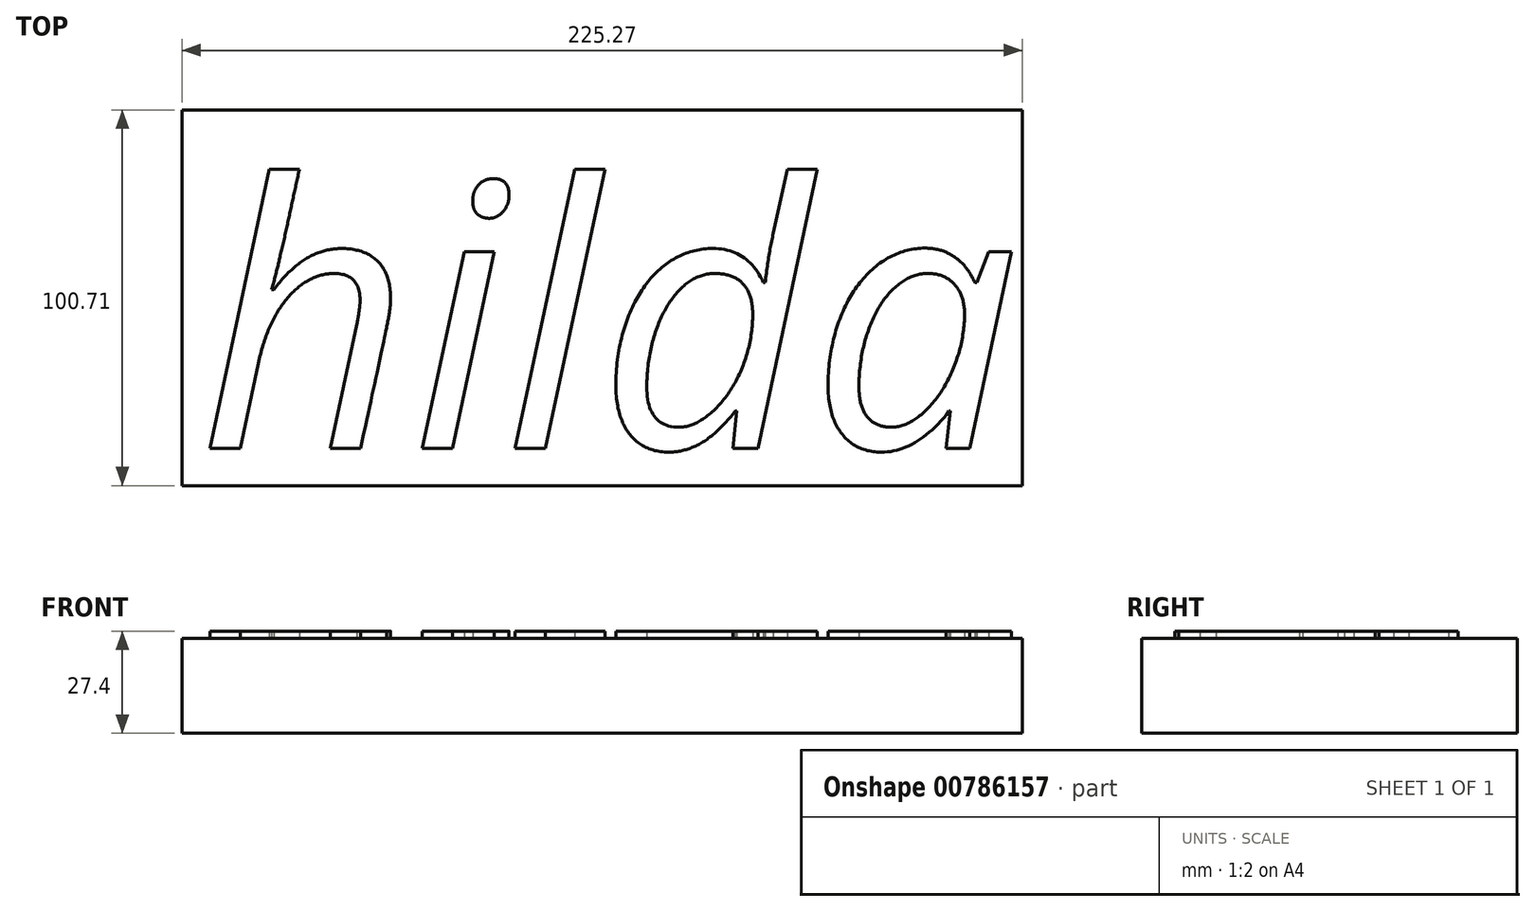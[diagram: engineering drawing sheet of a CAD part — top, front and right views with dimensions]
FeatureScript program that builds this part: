
annotation { "Feature Type Name" : "Feature", "Feature Type Description" : "" }
export const myFeature = defineFeature(function(context is Context, id is Id, definition is map)
    precondition{}
    {
        {
            var Q0;
            Q0=qCreatedBy(makeId("Top.planeOp"),FACE);
            var sketch = newSketch(context, id + "F0", { "sketchPlane" : qUnion([Q0])});
            skLineSegment(sketch, "E0.bottom", {"start": v(0, 0) * mm, "end": v(225.27, 0) * mm});
            skLineSegment(sketch, "E0.top", {"start": v(0, 100.71) * mm, "end": v(225.27, 100.71) * mm});
            skLineSegment(sketch, "E0.left", {"start": v(0, 0) * mm, "end": v(0, 100.71) * mm});
            skLineSegment(sketch, "E0.right", {"start": v(225.27, 0) * mm, "end": v(225.27, 100.71) * mm});
            skSolve(sketch);
        }
        {
            var Q0;
            Q0 = qSketchRegion(id + "F0", true);
            extrude(context, id + "F1", {"entities" : qUnion([Q0]), "depth" : 25.4 * mm, "offsetDistance" : 25.4 * mm});
        }
        {
            var Q0;
            Q0=makeQuery(id+"F1.opExtrude","CAP_FACE",FACE,{"disambiguationData":[OSD([sQuery(id+"F0.wireOp",EDGE,"E0.bottom"),sQuery(id+"F0.wireOp",EDGE,"E0.top"),sQuery(id+"F0.wireOp",EDGE,"E0.left"),sQuery(id+"F0.wireOp",EDGE,"E0.right")])],"isStart":false});
            var sketch = newSketch(context, id + "F2", { "sketchPlane" : qUnion([Q0])});
            skText(sketch, "E1", { "text": "hilda", "fontName": "OpenSans-Italic.ttf"});
            const initialGuessF2  = {"E1": [0.00465, 0.00994, 1, 0, 0.07097]};
            skSetInitialGuess(sketch, initialGuessF2);
            skSolve(sketch);
        }
        {
            var Q0;
            Q0 = qSketchRegion(id + "F2", true);
            extrude(context, id + "F3", {"entities" : qUnion([Q0]), "operationType" : NewBodyOperationType.ADD, "depth" : 2 * mm, "offsetDistance" : 25 * mm});
        }
    });
